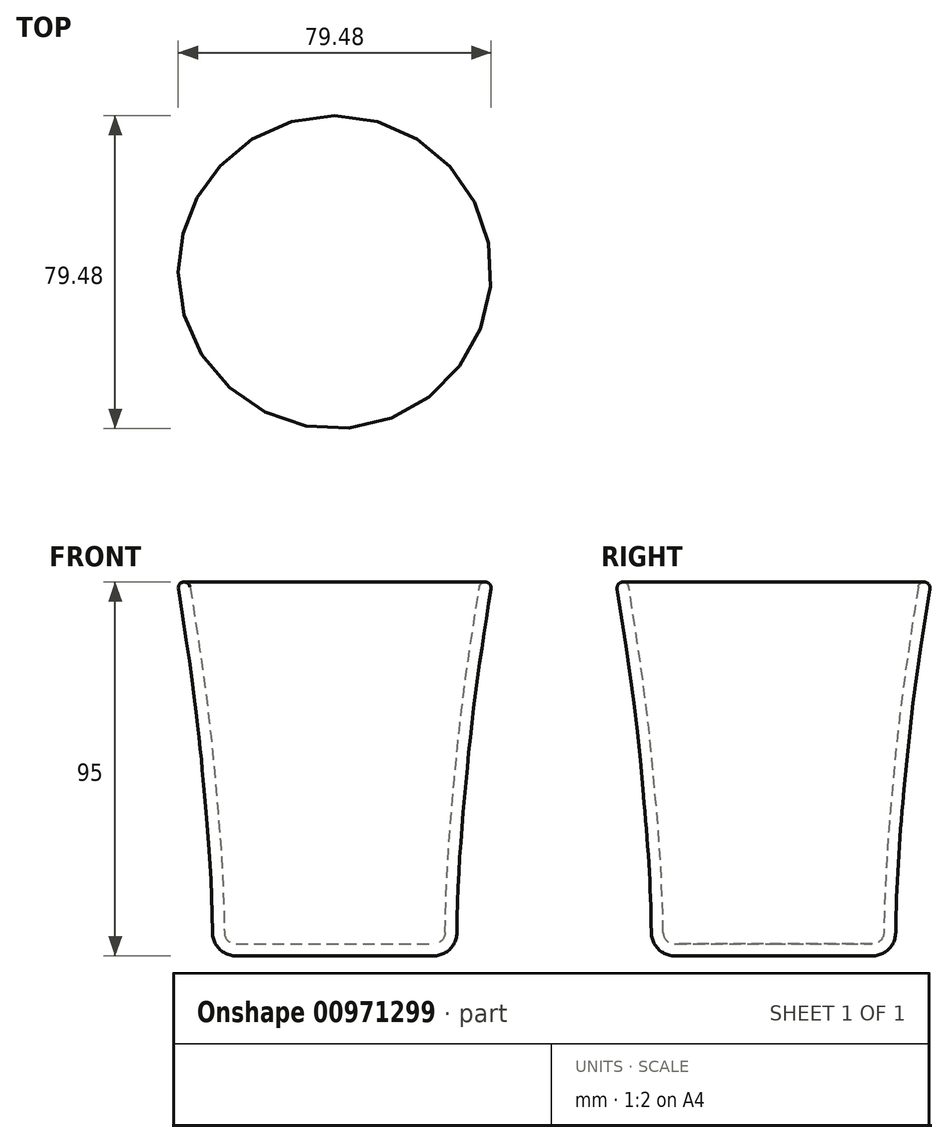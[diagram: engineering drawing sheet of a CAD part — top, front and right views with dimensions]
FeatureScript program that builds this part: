
annotation { "Feature Type Name" : "Feature", "Feature Type Description" : "" }
export const myFeature = defineFeature(function(context is Context, id is Id, definition is map)
    precondition{}
    {
        {
            var Q0;
            Q0=qCreatedBy(makeId("Front.planeOp"),FACE);
            var sketch = newSketch(context, id + "F0", { "sketchPlane" : qUnion([Q0])});
            skLineSegment(sketch, "E0", {"start": v(31, 0) * mm, "end": v(0, 0) * mm});
            skLineSegment(sketch, "E1", {"start": v(0, 0) * mm, "end": v(0, 95) * mm});
            skLineSegment(sketch, "E2", {"start": v(0, 95) * mm, "end": v(40, 95) * mm});
            skFitSpline(sketch, "E3", {"points": [v(31, 0) * mm, v(33.3, 43.33) * mm, v(40, 95) * mm], "startDerivative": vector(0.21, 129.92) * mm, "endDerivative": vector(29.23, 181.98) * mm});
            skSolve(sketch);
        }
        {
            var Q0;
            Q0=makeQuery(id+"F0.imprint","IMPRINT",FACE,{"disambiguationData":[TD([[makeQuery(id+"F0.imprint","IMPRINT",EDGE,{"derivedFrom":sQuery(id+"F0.wireOp",EDGE,"E0")}),-1.0]])]});
            var Q1;
            Q1=sQuery(id+"F0.wireOp",EDGE,"E1");
            revolve(context, id + "F1", {"surfaceOperationType" : NewSurfaceOperationType.NEW, "entities" : qUnion([Q0]), "axis" : qUnion([Q1]), "revolveType" : RevolveType.FULL});
        }
        {
            var Q0;
            Q0=makeQuery(id+"F1.opRevolve","SWEPT_EDGE",EDGE,{"disambiguationData":[OSD([sQuery(id+"F0.wireOp",EDGE,"E0"),sQuery(id+"F0.wireOp",EDGE,"E3")])]});
            fillet(context, id + "F2", {"entities" : qUnion([Q0]), "radius" : 6 * mm, "tangentPropagation" : true, "allowEdgeOverflow" : false});
        }
        {
            var Q0;
            Q0=makeQuery(id+"F1.opRevolve","SWEPT_FACE",FACE,{"disambiguationData":[OSD([sQuery(id+"F0.wireOp",EDGE,"E2")])]});
            shell(context, id + "F3", {"entities" : qUnion([Q0]), "thickness" : 3 * mm});
        }
        {
            var Q0;
            Q0=makeQuery(id+"F3.opShell","OFFSET_EDGE",EDGE,{"disambiguationData":[OSD([sQuery(id+"F0.wireOp",EDGE,"E2"),sQuery(id+"F0.wireOp",EDGE,"E3")])]});
            var Q1;
            Q1=makeQuery(id+"F1.opRevolve","SWEPT_EDGE",EDGE,{"disambiguationData":[OSD([sQuery(id+"F0.wireOp",EDGE,"E2"),sQuery(id+"F0.wireOp",EDGE,"E3")])]});
            fillet(context, id + "F4", {"entities" : qUnion([Q0, Q1]), "radius" : 1.5 * mm, "tangentPropagation" : true, "allowEdgeOverflow" : false});
        }
    });
